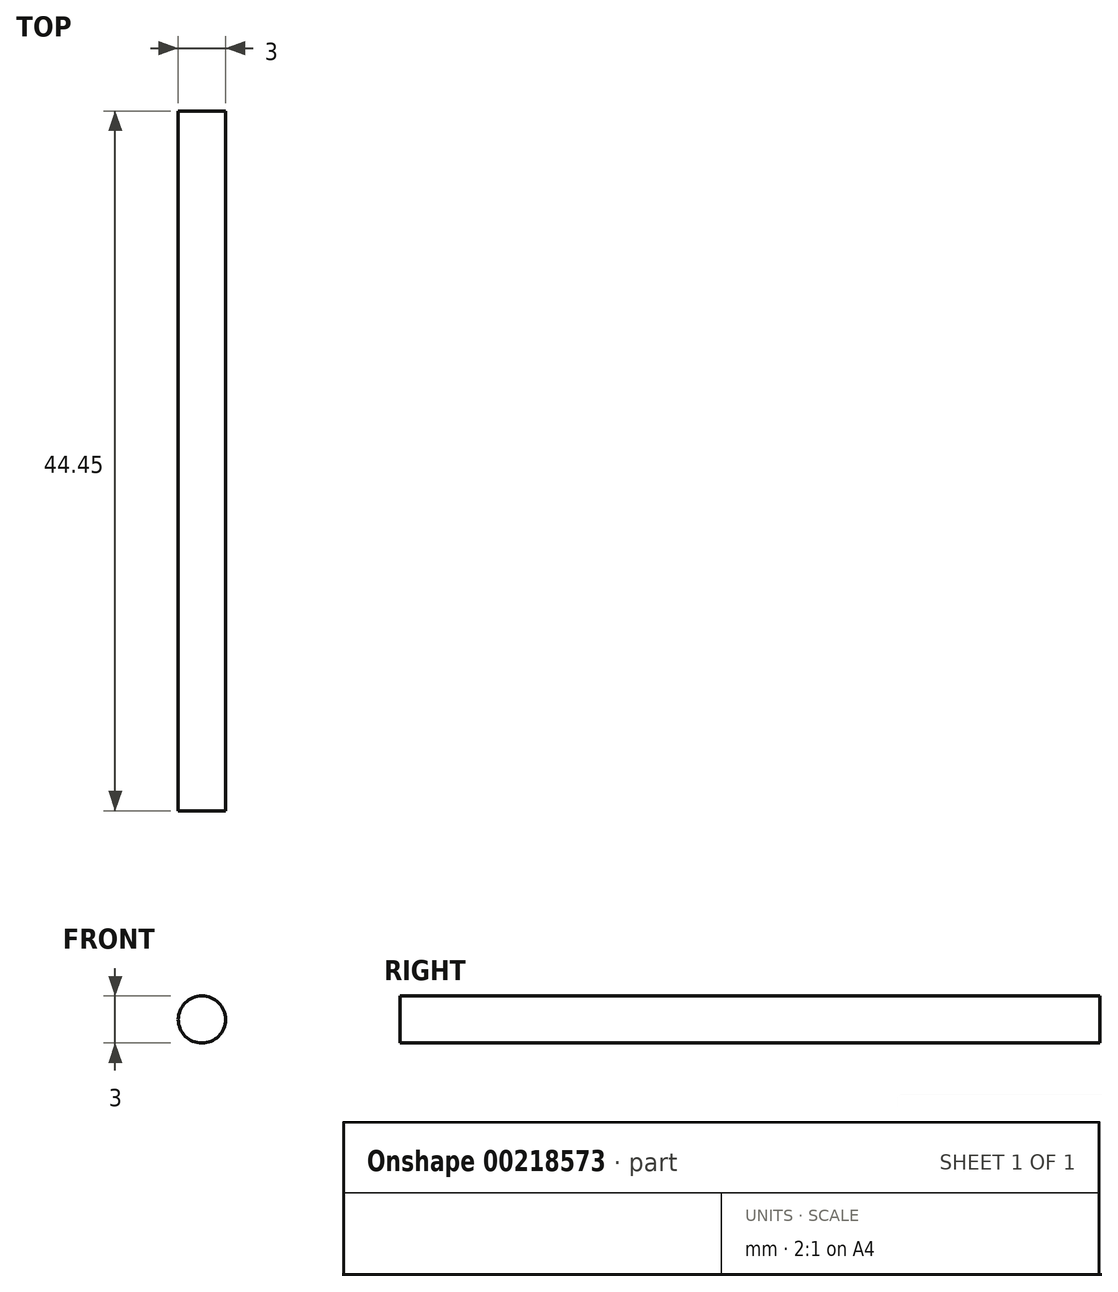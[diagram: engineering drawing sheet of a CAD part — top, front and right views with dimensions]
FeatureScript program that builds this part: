
annotation { "Feature Type Name" : "Feature", "Feature Type Description" : "" }
export const myFeature = defineFeature(function(context is Context, id is Id, definition is map)
    precondition{}
    {
        {
            var Q0;
            Q0=qCreatedBy(makeId("Front.planeOp"),FACE);
            var sketch = newSketch(context, id + "F0", { "sketchPlane" : qUnion([Q0])});
            skCircle(sketch, "E0", {"center": v(18.68, 12.5) * mm, "radius": 1.5 * mm});
            skSolve(sketch);
        }
        {
            var Q0;
            Q0=makeQuery(id+"F0.imprint","IMPRINT",FACE,{"disambiguationData":[TD([[makeQuery(id+"F0.imprint","IMPRINT",EDGE,{"derivedFrom":sQuery(id+"F0.wireOp",EDGE,"E0")}),1.0]])]});
            extrude(context, id + "F1", {"entities" : qUnion([Q0]), "depth" : 44.45 * mm});
        }
    });
